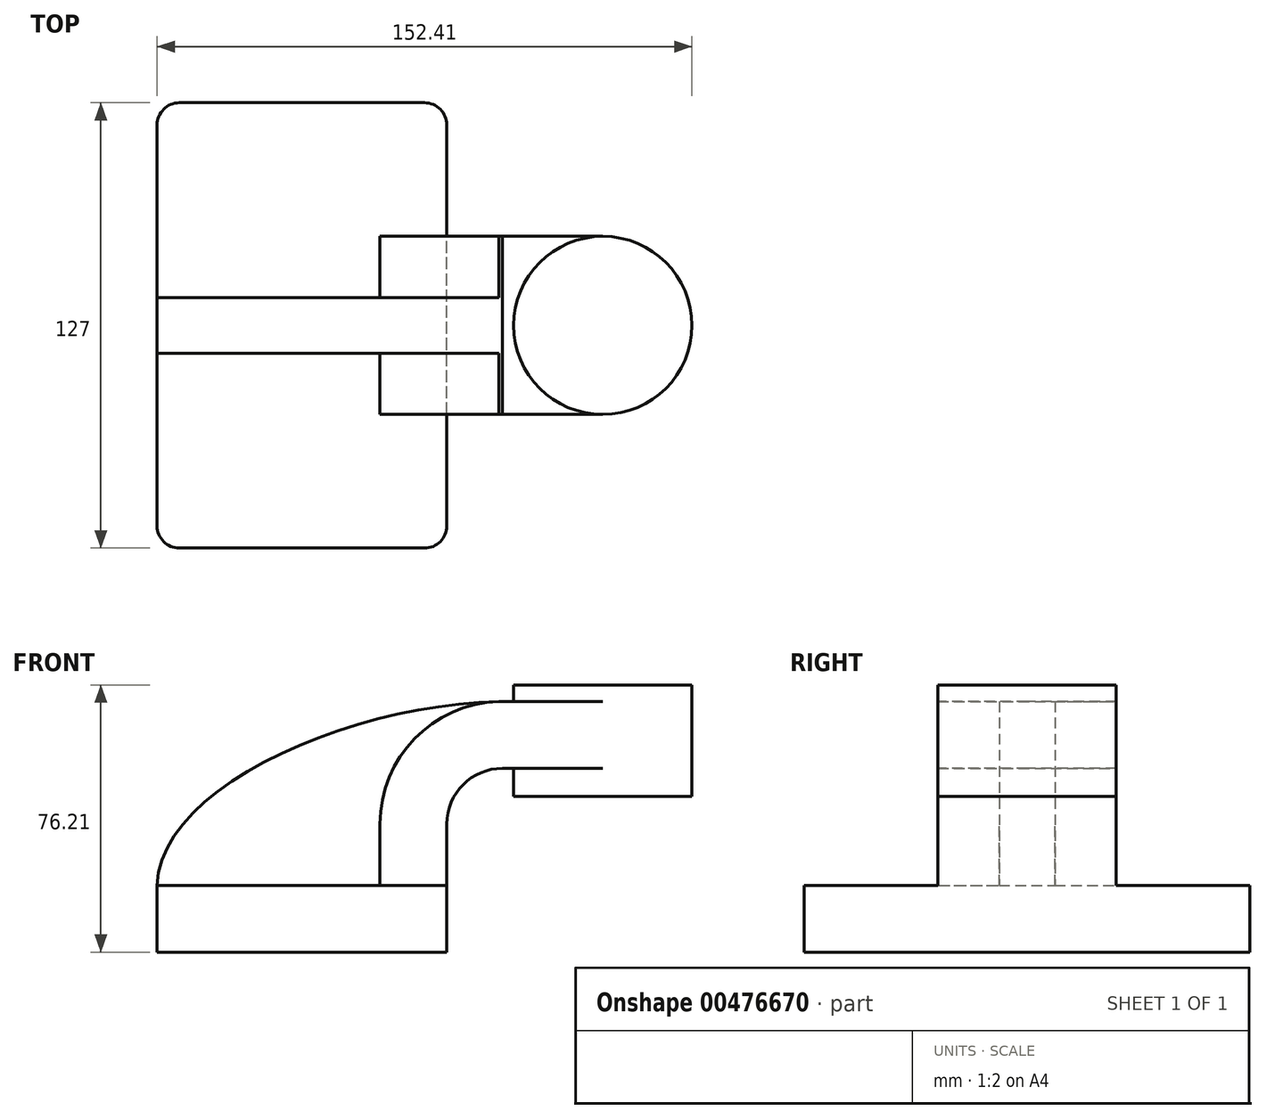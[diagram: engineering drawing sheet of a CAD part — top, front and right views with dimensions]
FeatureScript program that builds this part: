
annotation { "Feature Type Name" : "Feature", "Feature Type Description" : "" }
export const myFeature = defineFeature(function(context is Context, id is Id, definition is map)
    precondition{}
    {
        {
            var Q0;
            Q0=qCreatedBy(makeId("Front.planeOp"),FACE);
            var sketch = newSketch(context, id + "F0", { "sketchPlane" : qUnion([Q0])});
            skLineSegment(sketch, "E0.bottom", {"start": v(-41.28, 9.52) * mm, "end": v(41.27, 9.53) * mm});
            skLineSegment(sketch, "E0.top", {"start": v(-41.28, -9.53) * mm, "end": v(41.28, -9.53) * mm});
            skLineSegment(sketch, "E0.left", {"start": v(-41.28, 9.52) * mm, "end": v(-41.27, -9.53) * mm});
            skLineSegment(sketch, "E0.right", {"start": v(41.28, 9.53) * mm, "end": v(41.28, -9.52) * mm});
            skPoint(sketch, "E0.middle", {"position": v(0, 0) * mm});
            skLineSegment(sketch, "E1.bottom", {"start": v(111.12, 66.68) * mm, "end": v(60.32, 66.68) * mm});
            skLineSegment(sketch, "E1.top", {"start": v(111.12, 34.93) * mm, "end": v(60.32, 34.93) * mm});
            skLineSegment(sketch, "E1.left", {"start": v(111.12, 66.68) * mm, "end": v(111.12, 34.93) * mm});
            skLineSegment(sketch, "E1.right", {"start": v(60.32, 66.68) * mm, "end": v(60.32, 34.93) * mm});
            skPoint(sketch, "E1.middle", {"position": v(85.72, 50.8) * mm});
            skLineSegment(sketch, "E2", {"start": v(41.27, 9.53) * mm, "end": v(41.27, 27) * mm});
            skArc(sketch, "E3", {"start": v(41.27, 27) * mm, "mid": v(45.92, 38.23) * mm, "end": v(57.15, 42.88) * mm});
            skLineSegment(sketch, "E4", {"start": v(57.15, 42.88) * mm, "end": v(85.72, 42.88) * mm});
            skLineSegment(sketch, "E5.0", {"start": v(57.15, 61.93) * mm, "end": v(86.05, 61.93) * mm});
            skArc(sketch, "E5.1", {"start": v(22.22, 27) * mm, "mid": v(32.45, 51.7) * mm, "end": v(57.15, 61.93) * mm});
            skLineSegment(sketch, "E5.2", {"start": v(22.22, 9.53) * mm, "end": v(22.22, 27) * mm});
            skLineSegment(sketch, "E6", {"start": v(85.72, 34.93) * mm, "end": v(85.72, 66.68) * mm});
            skFitSpline(sketch, "E7", {"points": [v(57.15, 61.93) * mm, v(-41.28, 9.52) * mm], "startDerivative": vector(-128.92, -1.4) * mm, "endDerivative": vector(-1.92, -84.37) * mm});
            skPoint(sketch, "E8.1.internal.snap0", {"position": v(-41.28, 0) * mm});
            skSolve(sketch);
        }
        {
            var Q0;
            {var subQ0=sQuery(id+"F0.wireOp",EDGE,"E5.0");var subQ1=sQuery(id+"F0.wireOp",EDGE,"E1.right");var subQ2=makeQuery(id+"F0.imprint","INTERSECT",VERTEX,{"derivedFrom":[subQ1,subQ0]});Q0=makeQuery(id+"F0.imprint","IMPRINT",FACE,{"disambiguationData":[TD([[makeQuery(id+"F0.imprint","IMPRINT",EDGE,{"disambiguationData":[TD([[subQ2,-1.0]])],"derivedFrom":subQ1}),1.0]])]});}
            var Q1;
            {var subQ6=sQuery(id+"F0.wireOp",EDGE,"E2");Q1=makeQuery(id+"F0.imprint","IMPRINT",FACE,{"disambiguationData":[TD([[makeQuery(id+"F0.imprint","IMPRINT",EDGE,{"derivedFrom":subQ6}),1.0]])]});}
            extrude(context, id + "F1", {"entities" : qUnion([Q0, Q1]), "endBound" : BoundingType.SYMMETRIC, "depth" : 50.8 * mm});
        }
        {
            var Q0;
            Q0=makeQuery(id+"F0.imprint","IMPRINT",FACE,{"disambiguationData":[TD([[makeQuery(id+"F0.imprint","IMPRINT",EDGE,{"derivedFrom":sQuery(id+"F0.wireOp",EDGE,"E0.top")}),1.0]])]});
            extrude(context, id + "F2", {"entities" : qUnion([Q0]), "operationType" : NewBodyOperationType.ADD, "endBound" : BoundingType.SYMMETRIC, "depth" : 127 * mm});
        }
        {
            var Q0;
            {var subQ3=sQuery(id+"F0.wireOp",EDGE,"E5.2");Q0=makeQuery(id+"F0.imprint","IMPRINT",FACE,{"disambiguationData":[TD([[makeQuery(id+"F0.imprint","IMPRINT",EDGE,{"derivedFrom":subQ3}),1.0]])]});}
            extrude(context, id + "F3", {"entities" : qUnion([Q0]), "operationType" : NewBodyOperationType.ADD, "endBound" : BoundingType.SYMMETRIC, "depth" : 15.88 * mm});
        }
        {
            var Q0;
            {var subQ0=sQuery(id+"F0.wireOp",EDGE,"E1.left");Q0=makeQuery(id+"F0.imprint","IMPRINT",FACE,{"disambiguationData":[TD([[makeQuery(id+"F0.imprint","IMPRINT",EDGE,{"derivedFrom":subQ0}),-1.0]])]});}
            var Q1;
            Q1=sQuery(id+"F0.wireOp",EDGE,"E6");
            revolve(context, id + "F4", {"operationType" : NewBodyOperationType.ADD, "entities" : qUnion([Q0]), "axis" : qUnion([Q1]), "revolveType" : RevolveType.FULL});
        }
        {
            var Q0;
            Q0=makeQuery(id+"F2.opExtrude","CAP_EDGE",EDGE,{"disambiguationData":[OSD([sQuery(id+"F0.wireOp",EDGE,"E0.right")])],"isStart":false});
            var Q1;
            Q1=makeQuery(id+"F2.opExtrude","CAP_EDGE",EDGE,{"disambiguationData":[OSD([sQuery(id+"F0.wireOp",EDGE,"E0.left")])],"isStart":false});
            var Q2;
            Q2=makeQuery(id+"F2.opExtrude","CAP_EDGE",EDGE,{"disambiguationData":[OSD([sQuery(id+"F0.wireOp",EDGE,"E0.right")])],"isStart":true});
            var Q3;
            Q3=makeQuery(id+"F2.opExtrude","CAP_EDGE",EDGE,{"disambiguationData":[OSD([sQuery(id+"F0.wireOp",EDGE,"E0.left")])],"isStart":true});
            fillet(context, id + "F5", {"entities" : qUnion([Q0, Q1, Q2, Q3]), "radius" : 6.35 * mm, "tangentPropagation" : true, "allowEdgeOverflow" : false});
        }
    });
